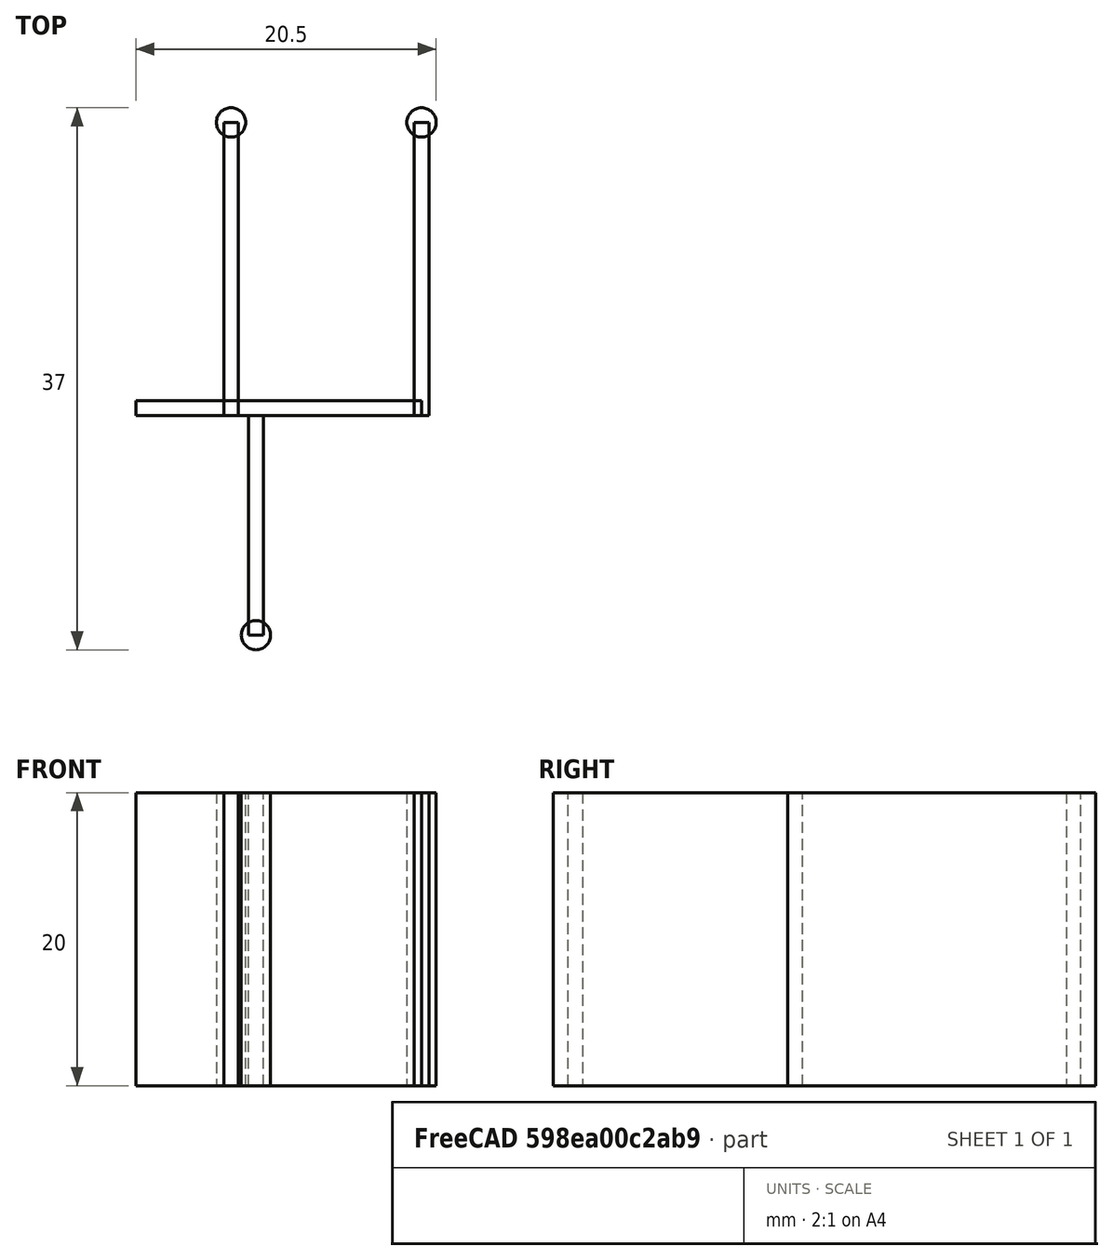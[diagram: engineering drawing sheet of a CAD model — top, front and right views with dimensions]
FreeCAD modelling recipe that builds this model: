
FCSTD DOCUMENT  (FreeCAD 1.0R39109 (Git))
Label: usb-holder-desk-v2
License: All rights reserved
LicenseURL: http://en.wikipedia.org/wiki/All_rights_reserved
objects: Part::Box×4, Part::Cylinder×3, Sketcher::SketchObject×1
note: 9 computed .brp shape members not serialized (recipe doc carries the construction recipe); baked Part::Feature solids carry a one-line shape summary decoded from their .brp

FEATURE [Sketcher::SketchObject] Sketch
  ArcFitTolerance = 0
  FullyConstrained = true
  MakeInternals = false
FEATURE [Part::Box] Box  label="Cube"
  AttacherType = Attacher::AttachEngine3D
  Height = 20
  Length = 19.5
  Width = 1
FEATURE [Part::Box] Box001  label="Cube001"
  AttacherType = Attacher::AttachEngine3D
  Height = 20
  Length = 1
  Placement = pos=(6,0,0) rot=(0,0,1;0rad)
  Width = 20
FEATURE [Part::Box] Box002  label="Cube002"
  AttacherType = Attacher::AttachEngine3D
  Height = 20
  Length = 1
  Placement = pos=(19,0,0) rot=(0,0,1;0rad)
  Width = 20
FEATURE [Part::Cylinder] Cylinder
  Angle = 360
  AttacherType = Attacher::AttachEngine3D
  FirstAngle = 0
  Height = 20
  Placement = pos=(6.5,20,0) rot=(0,0,1;0rad)
  Radius = 1
  SecondAngle = 0
FEATURE [Part::Cylinder] Cylinder001
  Angle = 360
  AttacherType = Attacher::AttachEngine3D
  FirstAngle = 0
  Height = 20
  Placement = pos=(19.5,20,0) rot=(0,0,1;0rad)
  Radius = 1
  SecondAngle = 0
FEATURE [Part::Box] Box003  label="Cube003"
  AttacherType = Attacher::AttachEngine3D
  Height = 20
  Length = 1
  Placement = pos=(7.7,-15,0) rot=(0,0,1;0rad)
  Width = 15
FEATURE [Part::Cylinder] Cylinder002
  Angle = 360
  AttacherType = Attacher::AttachEngine3D
  FirstAngle = 0
  Height = 20
  Placement = pos=(8.2,-15,0) rot=(0,0,1;0rad)
  Radius = 1
  SecondAngle = 0
